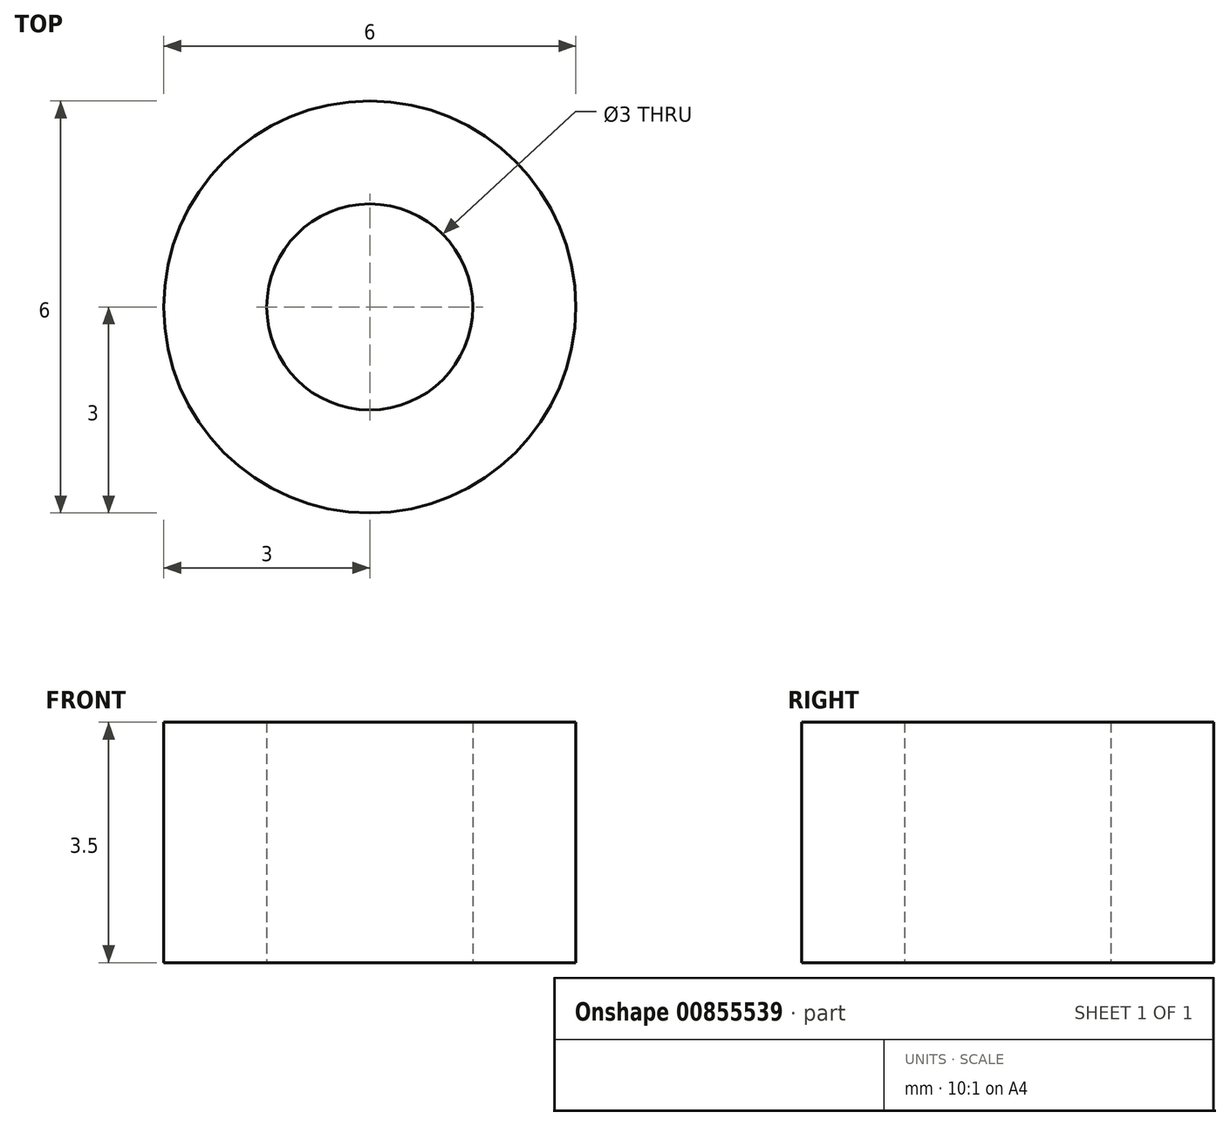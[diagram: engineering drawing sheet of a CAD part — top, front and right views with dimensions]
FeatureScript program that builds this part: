
annotation { "Feature Type Name" : "Feature", "Feature Type Description" : "" }
export const myFeature = defineFeature(function(context is Context, id is Id, definition is map)
    precondition{}
    {
        {
            var Q0;
            Q0=qCreatedBy(makeId("Top.planeOp"),FACE);
            var sketch = newSketch(context, id + "F0", { "sketchPlane" : qUnion([Q0])});
            skCircle(sketch, "E0", {"center": v(0, 0) * mm, "radius": 1.5 * mm});
            skCircle(sketch, "E1", {"center": v(0, 0) * mm, "radius": 3 * mm});
            skSolve(sketch);
        }
        {
            var Q0;
            Q0=makeQuery(id+"F0.imprint","IMPRINT",FACE,{"disambiguationData":[TD([[makeQuery(id+"F0.imprint","IMPRINT",EDGE,{"derivedFrom":sQuery(id+"F0.wireOp",EDGE,"E0")}),-1.0]])]});
            extrude(context, id + "F1", {"entities" : qUnion([Q0]), "depth" : 3.5 * mm, "offsetDistance" : 25 * mm});
        }
    });
